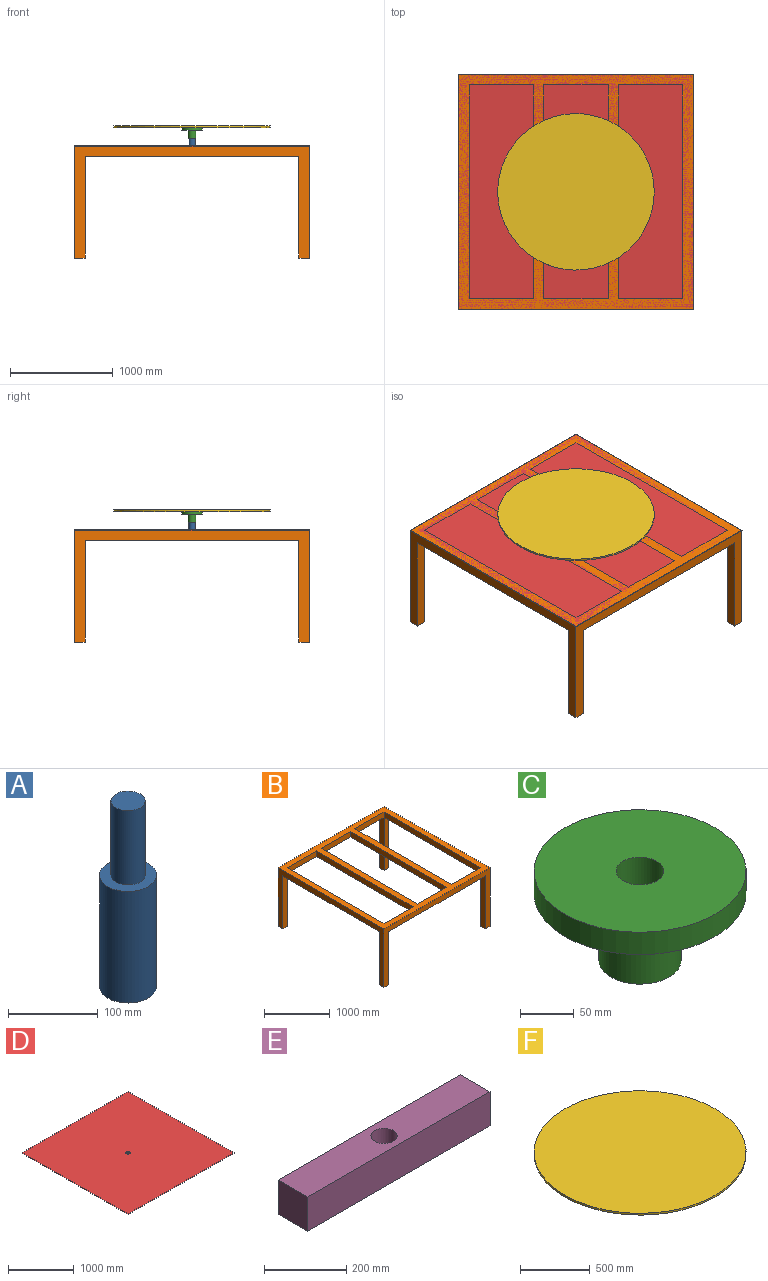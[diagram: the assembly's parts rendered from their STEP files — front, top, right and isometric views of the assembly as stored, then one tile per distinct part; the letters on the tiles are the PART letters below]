
ASSEMBLY  parts=6 mates=5
PART A: 5 faces, bbox 63.5x63.5x254 mm
  f0: cylinder r=31.75mm len=152.4mm, axis (0,0,-1), area 30402.4mm2, adj f1,f2
  f1: plane 63.5x63.5mm, normal (0,0,1), area 2026.8mm2, adj f0,f3
  f2: plane 63.5x63.5mm, normal (0,0,-1), area 3166.9mm2, adj f0
  f3: cylinder r=19.05mm len=101.6mm, axis (0,0,-1), area 12161mm2, adj f1,f4
  f4: plane 38.1x38.1mm, normal (0,0,1), area 1140.1mm2, adj f3
PART B: 32 faces, bbox 2286x2286x1092.2 mm
  f0: plane 2082.8x101.6mm, normal (0,0,-1), area 211612.5mm2, adj f13,f17,f23,f29
  f1: plane 2082.8x101.6mm, normal (0,0,-1), area 211612.5mm2, adj f3,f7,f20,f27
  f2: plane 2286x1092.2mm, normal (0,1,0), area 433547.5mm2, adj f3,f17,f18,f19,f26,f28,f30,f31
  f3: plane 2286x1092.2mm, normal (-1,0,0), area 433547.5mm2, adj f1,f2,f4,f18,f20,f22,f27,f28
  f4: plane 2286x1092.2mm, normal (0,-1,0), area 433547.5mm2, adj f3,f17,f18,f19,f21,f22,f24,f25
  f5: plane 2082.8x101.6mm, normal (-1,0,0), area 211612.5mm2, adj f6,f14,f18,f19
  f6: plane 626.36x101.6mm, normal (0,1,0), area 63638.6mm2, adj f5,f7,f18,f19
  f7: plane 2082.8x101.6mm, normal (1,0,0), area 211612.5mm2, adj f1,f6,f14,f18
  f8: plane 626.36x101.6mm, normal (0,1,0), area 63638.6mm2, adj f9,f15,f18,f19
  f9: plane 2082.8x101.6mm, normal (1,0,0), area 211612.5mm2, adj f8,f10,f18,f19
  f10: plane 626.36x101.6mm, normal (0,-1,0), area 63638.6mm2, adj f9,f15,f18,f19
  f11: plane 2082.8x101.6mm, normal (1,0,0), area 211612.5mm2, adj f12,f16,f18,f19
  f12: plane 626.87x101.6mm, normal (0,-1,0), area 63690.2mm2, adj f11,f13,f18,f19
  f13: plane 2082.8x101.6mm, normal (-1,0,0), area 211612.5mm2, adj f0,f12,f16,f18
  f14: plane 626.36x101.6mm, normal (0,-1,0), area 63638.6mm2, adj f5,f7,f18,f19
  f15: plane 2082.8x101.6mm, normal (-1,0,0), area 211612.5mm2, adj f8,f10,f18,f19
  f16: plane 626.87x101.6mm, normal (0,1,0), area 63690.2mm2, adj f11,f13,f18,f19
  f17: plane 2286x1092.2mm, normal (1,0,0), area 433547.5mm2, adj f0,f2,f4,f18,f23,f25,f29,f31
  f18: plane 2286x2286mm, normal (0,0,1), area 1310965.1mm2, adj f2,f3,f4,f5,f6,f7,f8,f9
  f19: plane 2286x2082.8mm, normal (0,0,-1), area 846449.9mm2, adj f2,f4,f5,f6,f8,f9,f10,f11
  f20: plane 990.6x101.6mm, normal (0,1,0), area 100645mm2, adj f1,f3,f21,f22
  f21: plane 990.6x101.6mm, normal (1,0,0), area 100645mm2, adj f4,f19,f20,f22
  f22: plane 101.6x101.6mm, normal (0,0,-1), area 10322.6mm2, adj f3,f4,f20,f21
  f23: plane 990.6x101.6mm, normal (0,1,0), area 100645mm2, adj f0,f17,f24,f25
  f24: plane 990.6x101.6mm, normal (-1,0,0), area 100645mm2, adj f4,f19,f23,f25
  f25: plane 101.6x101.6mm, normal (0,0,-1), area 10322.6mm2, adj f4,f17,f23,f24
  f26: plane 990.6x101.6mm, normal (1,0,0), area 100645mm2, adj f2,f19,f27,f28
  f27: plane 990.6x101.6mm, normal (0,-1,0), area 100645mm2, adj f1,f3,f26,f28
  f28: plane 101.6x101.6mm, normal (0,0,-1), area 10322.6mm2, adj f2,f3,f26,f27
  f29: plane 990.6x101.6mm, normal (0,-1,0), area 100645mm2, adj f0,f17,f30,f31
  f30: plane 990.6x101.6mm, normal (-1,0,0), area 100645mm2, adj f2,f19,f29,f31
  f31: plane 101.6x101.6mm, normal (0,0,-1), area 10322.6mm2, adj f2,f17,f29,f30
PART C: 6 faces, bbox 196.9x196.9x101.6 mm
  f0: cylinder r=38.1mm len=76.2mm, axis (0,0,-1), area 18241.5mm2, adj f1,f4
  f1: plane 76.2x76.2mm, normal (0,0,-1), area 3008.6mm2, adj f0,f5
  f2: cylinder r=98.42mm len=196.85mm, axis (0,0,-1), area 15707.9mm2, adj f3,f4
  f3: plane 196.85x196.85mm, normal (0,0,1), area 28882.3mm2, adj f2,f5
  f4: plane 196.85x196.85mm, normal (0,0,-1), area 25873.8mm2, adj f0,f2
  f5: cylinder r=22.23mm len=101.6mm, axis (0,0,1), area 14187.8mm2, adj f1,f3
PART D: 7 faces, bbox 2286x2286x6.4 mm
  f0: plane 2286x6.35mm, normal (0,1,0), area 14516.1mm2, adj f1,f3,f4,f5
  f1: plane 2286x6.35mm, normal (-1,0,0), area 14516.1mm2, adj f0,f2,f4,f5
  f2: plane 2286x6.35mm, normal (0,-1,0), area 14516.1mm2, adj f1,f3,f4,f5
  f3: plane 2286x6.35mm, normal (1,0,0), area 14516.1mm2, adj f0,f2,f4,f5
  f4: plane 2286x2286mm, normal (0,0,1), area 5222629.1mm2, adj f0,f1,f2,f3,f6
  f5: plane 2286x2286mm, normal (0,0,-1), area 5222629.1mm2, adj f0,f1,f2,f3,f6
  f6: cylinder r=31.75mm len=63.5mm, axis (0,0,1), area 1266.8mm2, adj f4,f5
PART E: 7 faces, bbox 626.5x101.6x101.6 mm
  f0: plane 626.52x101.6mm, normal (0,1,0), area 63654.1mm2, adj f1,f4,f5,f6
  f1: plane 101.6x101.6mm, normal (-1,0,0), area 10322.6mm2, adj f0,f2,f5,f6
  f2: plane 626.52x101.6mm, normal (0,-1,0), area 63654.1mm2, adj f1,f4,f5,f6
  f3: cylinder r=31.75mm len=101.6mm, axis (0,0,-1), area 20268.3mm2, adj f5,f6
  f4: plane 101.6x101.6mm, normal (1,0,0), area 10322.6mm2, adj f0,f2,f5,f6
  f5: plane 626.52x101.6mm, normal (0,0,1), area 60487.1mm2, adj f0,f1,f2,f3,f4
  f6: plane 626.52x101.6mm, normal (0,0,-1), area 60487.1mm2, adj f0,f1,f2,f3,f4
PART F: 3 faces, bbox 1524x1524x15.9 mm
  f0: cylinder r=762mm len=1524mm, axis (0,0,-1), area 76006.1mm2, adj f1,f2
  f1: plane 1524x1524mm, normal (0,0,1), area 1824146.9mm2, adj f0
  f2: plane 1524x1524mm, normal (0,0,-1), area 1824146.9mm2, adj f0
PLACE A t=(-945.72,-584.46,805.93)mm
PLACE B t=(155.69,-1686.99,780.53)mm fixed
PLACE C t=(-945.72,-584.46,958.33)mm
PLACE D t=(140.06,-1680.85,875.78)mm
PLACE E t=(-729.48,-603.9,780.53)mm
PLACE F t=(-945.72,-584.46,1059.93)mm
MATE fastened F.f0 <-> C.f2  axis (0,0,-1) through (-945.72,-584.46,1059.93)mm
MATE fastened A.f0 <-> D.f6  axis (0,0,-1) through (-945.72,-584.46,805.93)mm
MATE fastened D.f2 <-> B.f4  axis (0,-1,0) through (-945.72,-1727.46,882.13)mm
MATE fastened C.f5 <-> A.f3  axis (0,0,1) through (-945.72,-584.46,1059.93)mm
MATE fastened E.f5 <-> B.f18  axis (0,0,1) through (-1259.16,-584.46,882.13)mm
